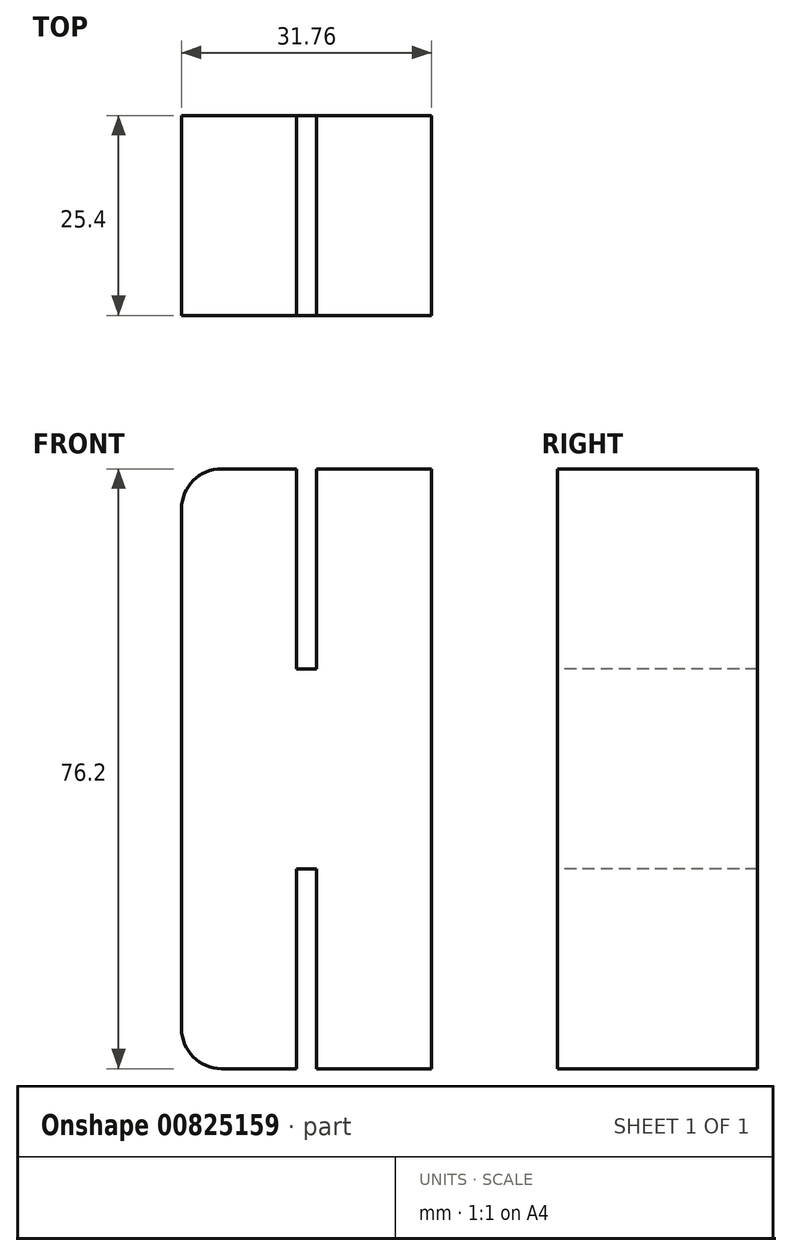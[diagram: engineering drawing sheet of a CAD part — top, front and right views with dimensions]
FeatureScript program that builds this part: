
annotation { "Feature Type Name" : "Feature", "Feature Type Description" : "" }
export const myFeature = defineFeature(function(context is Context, id is Id, definition is map)
    precondition{}
    {
        {
            var Q0;
            Q0=qCreatedBy(makeId("Front.planeOp"),FACE);
            var sketch = newSketch(context, id + "F0", { "sketchPlane" : qUnion([Q0])});
            skLineSegment(sketch, "E0.bottom", {"start": v(15.88, 38.1) * mm, "end": v(-15.87, 38.1) * mm});
            skLineSegment(sketch, "E0.top", {"start": v(15.87, -38.1) * mm, "end": v(-15.88, -38.1) * mm});
            skLineSegment(sketch, "E0.left", {"start": v(15.88, 38.1) * mm, "end": v(15.87, -38.1) * mm});
            skLineSegment(sketch, "E0.right", {"start": v(-15.88, 38.1) * mm, "end": v(-15.88, -38.1) * mm});
            skPoint(sketch, "E0.middle", {"position": v(0, 0) * mm});
            skSolve(sketch);
        }
        {
            var Q0;
            Q0 = qSketchRegion(id + "F0", true);
            extrude(context, id + "F1", {"entities" : qUnion([Q0]), "depth" : 25.4 * mm, "offsetDistance" : 25.4 * mm});
        }
        {
            var Q0;
            Q0=makeQuery(id+"F1.opExtrude","CAP_FACE",FACE,{"disambiguationData":[OSD([sQuery(id+"F0.wireOp",EDGE,"E0.bottom"),sQuery(id+"F0.wireOp",EDGE,"E0.top"),sQuery(id+"F0.wireOp",EDGE,"E0.left"),sQuery(id+"F0.wireOp",EDGE,"E0.right")])],"isStart":false});
            var sketch = newSketch(context, id + "F2", { "sketchPlane" : qUnion([Q0])});
            skLineSegment(sketch, "E1.bottom", {"start": v(-1.27, 38.1) * mm, "end": v(1.27, 38.1) * mm});
            skLineSegment(sketch, "E1.top", {"start": v(-1.27, 12.7) * mm, "end": v(1.27, 12.7) * mm});
            skLineSegment(sketch, "E1.left", {"start": v(-1.27, 38.1) * mm, "end": v(-1.27, 12.7) * mm});
            skLineSegment(sketch, "E1.right", {"start": v(1.27, 38.1) * mm, "end": v(1.27, 12.7) * mm});
            skPoint(sketch, "E2", {"position": v(0, 12.7) * mm});
            skLineSegment(sketch, "E3", {"start": v(-15.88, 0) * mm, "end": v(15.88, 0) * mm, "construction": true});
            skLineSegment(sketch, "E4.MirrorCS", {"start": v(1.27, -38.1) * mm, "end": v(1.27, -12.7) * mm});
            skLineSegment(sketch, "E5.MirrorCS", {"start": v(-1.27, -38.1) * mm, "end": v(-1.27, -12.7) * mm});
            skLineSegment(sketch, "E6.MirrorCS", {"start": v(-1.27, -38.1) * mm, "end": v(1.27, -38.1) * mm});
            skLineSegment(sketch, "E7.MirrorCS", {"start": v(-1.27, -12.7) * mm, "end": v(1.27, -12.7) * mm});
            skSolve(sketch);
        }
        {
            var Q0;
            Q0=makeQuery(id+"F2.imprint","IMPRINT",FACE,{"disambiguationData":[TD([[makeQuery(id+"F2.imprint","IMPRINT",EDGE,{"derivedFrom":sQuery(id+"F2.wireOp",EDGE,"E1.bottom")}),1.0]])]});
            var Q1;
            Q1=makeQuery(id+"F2.imprint","IMPRINT",FACE,{"disambiguationData":[TD([[makeQuery(id+"F2.imprint","IMPRINT",EDGE,{"derivedFrom":sQuery(id+"F2.wireOp",EDGE,"E4.MirrorCS")}),1.0]])]});
            extrude(context, id + "F3", {"entities" : qUnion([Q0, Q1]), "operationType" : NewBodyOperationType.REMOVE, "oppositeDirection" : true, "depth" : 25.4 * mm, "offsetDistance" : 25.4 * mm});
        }
        {
            var Q0;
            Q0=makeQuery(id+"F1.opExtrude","SWEPT_EDGE",EDGE,{"disambiguationData":[OSD([sQuery(id+"F0.wireOp",EDGE,"E0.bottom"),sQuery(id+"F0.wireOp",EDGE,"E0.right")])]});
            var Q1;
            Q1=makeQuery(id+"F1.opExtrude","SWEPT_EDGE",EDGE,{"disambiguationData":[OSD([sQuery(id+"F0.wireOp",EDGE,"E0.top"),sQuery(id+"F0.wireOp",EDGE,"E0.right")])]});
            fillet(context, id + "F4", {"entities" : qUnion([Q0, Q1]), "radius" : 5.08 * mm, "tangentPropagation" : true, "allowEdgeOverflow" : false});
        }
    });
